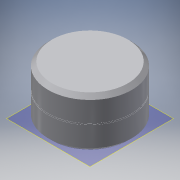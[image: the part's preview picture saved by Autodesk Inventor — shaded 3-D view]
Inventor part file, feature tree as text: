
AUTODESK INVENTOR PART (.ipt)
format: ipt  version: 2016 (Build 200138000, 138)  size: 238,592 bytes
history: native  units: in
note: dims shown in document units (in); Inventor stores cm internally (conversion verified against a paired STEP export)
features: thread x8, sketch x5, extrude x4, hole x2, plane x2, split x2, chamfer x1, revolve x1
ambient origin geometry x8: Origin, YZ Plane, XZ Plane, XY Plane, X Axis, Y Axis, Z Axis, Center Point
bodies: Solid1 (feature_tree), Solid2 (feature_tree), Solid3 (feature_tree)
feature tree (25):
  extrude  "Extrusion1"  Depth=1.5157in TaperAngle=0.0deg
  extrude  "Extrusion2"  Depth=0.9213in TaperAngle=0.0deg
  chamfer  "Chamfer1"  Distance=0.1181in Angle=45.0deg
  sketch  "Sketch3"  dims[d10=0.4134in d14=0.2264in d15=0.2264in d16=1.1811in d17=1.1811in]
  hole  "Hole1"  [1 undecoded]
  thread  "Thread1"  [1 undecoded]
  thread  "Thread2"  [1 undecoded]
  thread  "Thread3"  [1 undecoded]
  thread  "Thread4"  [1 undecoded]
  extrude  "Extrusion3"  Depth=0.3937in TaperAngle=0.0deg
  hole  "Hole2"  [1 undecoded]
  thread  "Thread5"  [1 undecoded]
  thread  "Thread6"  [1 undecoded]
  thread  "Thread7"  [1 undecoded]
  thread  "Thread8"  [1 undecoded]
  plane  "Work Plane1"
  sketch  "Sketch4"  dims[d18=0.0984in d19=0.2362in d20=0.1575in d21=0.0787in d22=90.0deg d23=0.1575in d24=0.8108in d25=0.3937in d26=0.0in]
  extrude  "Extrusion5"  Depth=0.3937in TaperAngle=0.0deg
  revolve  "Revolution4"  [1 undecoded]
  plane  "Work Plane2"
  split  "Split1"
  split  "Split2"
  sketch  "Sketch1"  dims[d0=2.5591in d1=1.5157in d2=0.0in]
  sketch  "Sketch2"  dims[d3=2.0079in d4=0.9213in d5=0.0in d7=0.1181in d8=0.0787in d9=45.0deg]
  sketch  "Sketch6"  dims[d27=0.3937in d28=0.0in d29=0.3937in d30=0.0in d31=0.3937in d32=0.0in d33=0.4724in d34=0.0in d35=0.4449in d36=0.4449in d37=0.0827in d38=0.2362in d39=0.1575in d40=0.0787in d41=90.0deg d42=0.1181in d43=0.8108in d44=0.3937in d45=0.0in d46=0.3937in d47=0.0in d48=0.3937in d49=0.0in d50=0.3937in d51=0.0in d52=1.6339in d53=0.0394in d54=0.7874in d56=0.5906in d57=0.5906in d58=0.5in d59=0.5in d62=0.5906in d63=0.0in d83=0.6398in d84=0.0197in d85=0.0197in d86=0.0098in d87=0.0098in d88=0.0098in d89=0.0098in d90=1.7178in d91=0.0in]
note: 11 required parameter values undecoded (feature->parameter linkage not recoverable at this tier; creation-order binding heuristic only, values carry confidence <= 0.55)